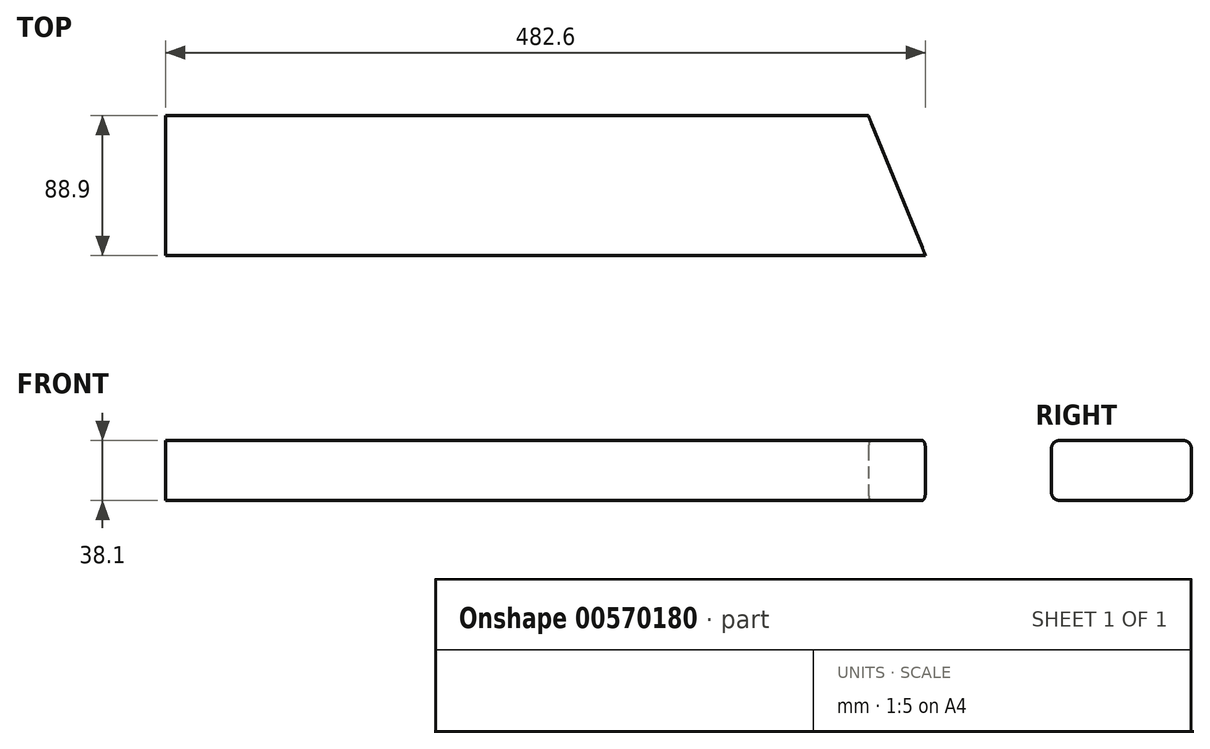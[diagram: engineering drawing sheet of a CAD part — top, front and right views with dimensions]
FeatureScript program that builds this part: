
annotation { "Feature Type Name" : "Feature", "Feature Type Description" : "" }
export const myFeature = defineFeature(function(context is Context, id is Id, definition is map)
    precondition{}
    {
        {
            var Q0;
            Q0=qCreatedBy(makeId("Top.planeOp"),FACE);
            var sketch = newSketch(context, id + "F0", { "sketchPlane" : qUnion([Q0])});
            skLineSegment(sketch, "E0", {"start": v(0, 88.9) * mm, "end": v(0, 0) * mm});
            skLineSegment(sketch, "E1", {"start": v(0, 0) * mm, "end": v(482.6, 0) * mm});
            skLineSegment(sketch, "E2", {"start": v(482.6, 0) * mm, "end": v(446.32, 88.9) * mm});
            skLineSegment(sketch, "E3", {"start": v(446.32, 88.9) * mm, "end": v(0, 88.9) * mm});
            skSolve(sketch);
        }
        {
            var Q0;
            Q0=makeQuery(id+"F0.imprint","IMPRINT",FACE,{"disambiguationData":[TD([[makeQuery(id+"F0.imprint","IMPRINT",EDGE,{"derivedFrom":sQuery(id+"F0.wireOp",EDGE,"E0")}),1.0]])]});
            extrude(context, id + "F1", {"entities" : qUnion([Q0]), "depth" : 38.1 * mm, "offsetDistance" : 25.4 * mm});
        }
        {
            var Q0;
            Q0=makeQuery(id+"F1.opExtrude","CAP_EDGE",EDGE,{"disambiguationData":[OSD([sQuery(id+"F0.wireOp",EDGE,"E3")])],"isStart":false});
            var Q1;
            Q1=makeQuery(id+"F1.opExtrude","CAP_EDGE",EDGE,{"disambiguationData":[OSD([sQuery(id+"F0.wireOp",EDGE,"E1")])],"isStart":false});
            var Q2;
            Q2=makeQuery(id+"F1.opExtrude","CAP_EDGE",EDGE,{"disambiguationData":[OSD([sQuery(id+"F0.wireOp",EDGE,"E3")])],"isStart":true});
            var Q3;
            Q3=makeQuery(id+"F1.opExtrude","CAP_EDGE",EDGE,{"disambiguationData":[OSD([sQuery(id+"F0.wireOp",EDGE,"E1")])],"isStart":true});
            fillet(context, id + "F2", {"entities" : qUnion([Q0, Q1, Q2, Q3]), "radius" : 5.08 * mm, "tangentPropagation" : true, "allowEdgeOverflow" : false});
        }
    });
